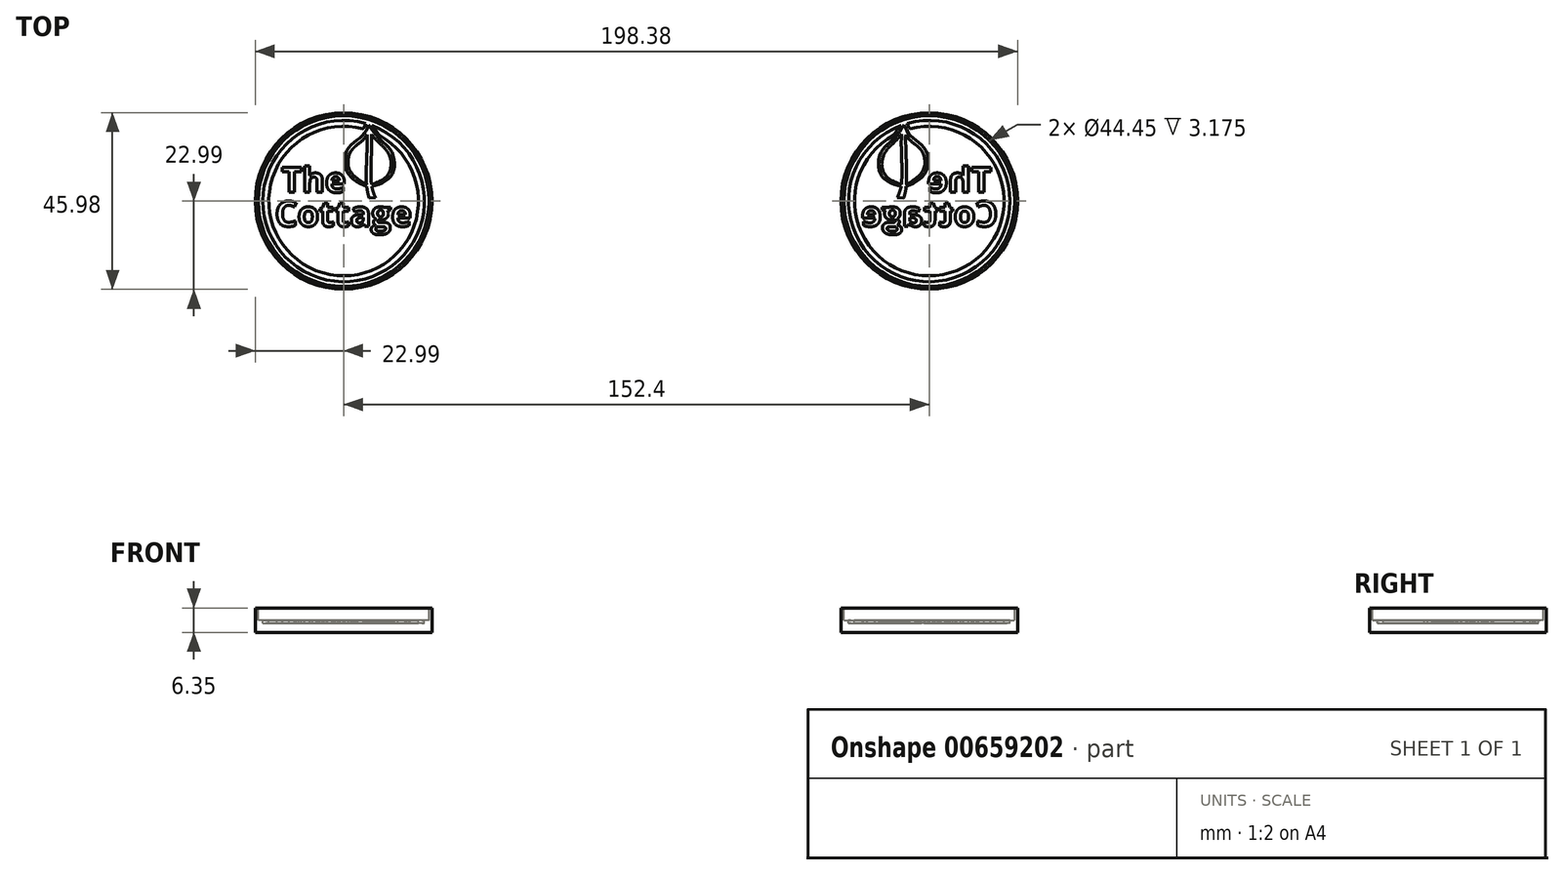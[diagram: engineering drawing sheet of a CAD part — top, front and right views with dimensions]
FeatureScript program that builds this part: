
annotation { "Feature Type Name" : "Feature", "Feature Type Description" : "" }
export const myFeature = defineFeature(function(context is Context, id is Id, definition is map)
    precondition{}
    {
        {
            var Q0;
            Q0=qCreatedBy(makeId("Top.planeOp"),FACE);
            var sketch = newSketch(context, id + "F0", { "sketchPlane" : qUnion([Q0])});
            skCircle(sketch, "E0", {"center": v(0, 0) * mm, "radius": 22.99 * mm});
            skSolve(sketch);
        }
        {
            var Q0;
            Q0 = qSketchRegion(id + "F0", true);
            extrude(context, id + "F1", {"entities" : qUnion([Q0]), "depth" : 6.35 * mm, "offsetDistance" : 25.4 * mm});
        }
        {
            var Q0;
            Q0=makeQuery(id+"F1.opExtrude","CAP_FACE",FACE,{"disambiguationData":[OSD([sQuery(id+"F0.wireOp",EDGE,"E0")])],"isStart":false});
            var sketch = newSketch(context, id + "F2", { "sketchPlane" : qUnion([Q0])});
            skCircle(sketch, "E1", {"center": v(0, 0) * mm, "radius": 22.23 * mm});
            skSolve(sketch);
        }
        {
            var Q0;
            Q0 = qSketchRegion(id + "F2", true);
            extrude(context, id + "F3", {"entities" : qUnion([Q0]), "operationType" : NewBodyOperationType.REMOVE, "oppositeDirection" : true, "depth" : 3.17 * mm, "offsetDistance" : 25.4 * mm});
        }
        {
            var Q0;
            Q0=makeQuery(id+"F3.boolean.opBoolean","COPY",FACE,{"derivedFrom":makeQuery(id+"F3.opExtrude","CAP_FACE",FACE,{"disambiguationData":[OSD([sQuery(id+"F2.wireOp",EDGE,"E1")])],"isStart":false})});
            var sketch = newSketch(context, id + "F4", { "sketchPlane" : qUnion([Q0])});
            skText(sketch, "E2", { "text": "The", "fontName": "OpenSans-Bold.ttf"});
            skText(sketch, "E3", { "text": "Cottage", "fontName": "OpenSans-Bold.ttf"});
            const initialGuessF4  = {"E2": [-0.01619, 0.00224, 1, 0, 0.0066], "E3": [-0.01786, -0.0066, 1, 0, 0.0066]};
            skSetInitialGuess(sketch, initialGuessF4);
            skSolve(sketch);
        }
        {
            var Q0;
            Q0 = qSketchRegion(id + "F4", true);
            extrude(context, id + "F5", {"entities" : qUnion([Q0]), "operationType" : NewBodyOperationType.REMOVE, "oppositeDirection" : true, "depth" : 0.76 * mm, "offsetDistance" : 25.4 * mm});
        }
        {
            var Q0;
            {var subQ0=sQuery(id+"F2.wireOp",EDGE,"E1");Q0=makeQuery(id+"F5.boolean.opBoolean","SPLIT",FACE,{"disambiguationData":[TD([makeQuery(id+"F3.boolean.opBoolean","COPY",FACE,{"derivedFrom":makeQuery(id+"F3.opExtrude","SWEPT_FACE",FACE,{"disambiguationData":[OSD([subQ0])]})})])],"derivedFrom":makeQuery(id+"F3.boolean.opBoolean","COPY",FACE,{"derivedFrom":makeQuery(id+"F3.opExtrude","CAP_FACE",FACE,{"disambiguationData":[OSD([subQ0])],"isStart":false})})});}
            var sketch = newSketch(context, id + "F6", { "sketchPlane" : qUnion([Q0])});
            skFitSpline(sketch, "E4", {"points": [v(5.96, 4.32) * mm, v(1.57, 8.06) * mm, v(1.84, 12.88) * mm, v(4.83, 15.75) * mm, v(6.61, 18.2) * mm], "startDerivative": vector(-18.93, 11.04) * mm, "endDerivative": vector(7.24, 12.22) * mm});
            skFitSpline(sketch, "E5", {"points": [v(8.3, 0.96) * mm, v(7.26, 4.32) * mm, v(7.26, 14.02) * mm, v(7.22, 17.4) * mm], "startDerivative": vector(-4.54, 9.79) * mm, "endDerivative": vector(-0.46, 10.19) * mm});
            skFitSpline(sketch, "E6", {"points": [v(8.3, 0.96) * mm, v(6.67, 0.74) * mm], "startDerivative": vector(-1.63, -0.22) * mm, "endDerivative": vector(-1.63, -0.22) * mm});
            skFitSpline(sketch, "E7", {"points": [v(7.22, 12.38) * mm, v(8.3, 13.58) * mm, v(8.98, 15.46) * mm], "startDerivative": vector(2.5, 2.3) * mm, "endDerivative": vector(1.04, 3.83) * mm});
            skFitSpline(sketch, "E8", {"points": [v(9.55, 14.9) * mm, v(9.05, 13.1) * mm, v(7.17, 11.15) * mm], "startDerivative": vector(-0.57, -4.06) * mm, "endDerivative": vector(-4.08, -3.46) * mm});
            skFitSpline(sketch, "E9", {"points": [v(7.1, 8.17) * mm, v(9.87, 10.39) * mm, v(11.25, 13.03) * mm], "startDerivative": vector(5.9, 3.93) * mm, "endDerivative": vector(2.29, 5.79) * mm});
            skFitSpline(sketch, "E10", {"points": [v(7.1, 7.13) * mm, v(9.65, 8.76) * mm, v(11.92, 11.85) * mm], "startDerivative": vector(5.64, 2.92) * mm, "endDerivative": vector(4, 6.45) * mm});
            skFitSpline(sketch, "E11", {"points": [v(6.06, 12.44) * mm, v(4.12, 14.02) * mm, v(3.6, 14.73) * mm], "startDerivative": vector(-3.62, 2.7) * mm, "endDerivative": vector(-1.1, 1.78) * mm});
            skFitSpline(sketch, "E12", {"points": [v(6.06, 11.15) * mm, v(4.5, 12.44) * mm, v(2.78, 14.02) * mm], "startDerivative": vector(-3.2, 2.6) * mm, "endDerivative": vector(-3.36, 3.13) * mm});
            skFitSpline(sketch, "E13", {"points": [v(5.91, 8.27) * mm, v(3.73, 9.84) * mm, v(1.62, 12.44) * mm], "startDerivative": vector(-4.78, 2.94) * mm, "endDerivative": vector(-3.85, 5.36) * mm});
            skFitSpline(sketch, "E14", {"points": [v(5.9, 7.13) * mm, v(3.33, 8.9) * mm, v(1.27, 11.4) * mm], "startDerivative": vector(-5.46, 3.24) * mm, "endDerivative": vector(-3.8, 5.3) * mm});
            skFitSpline(sketch, "E15.trimOffspring", {"points": [v(6.11, 17.34) * mm, v(6.11, 14.02) * mm, v(5.96, 4.32) * mm, v(6.67, 0.74) * mm], "startDerivative": vector(0.25, -10.14) * mm, "endDerivative": vector(3.15, -10.45) * mm});
            skFitSpline(sketch, "E16", {"points": [v(6.01, 3.77) * mm, v(7.34, 3.82) * mm], "startDerivative": vector(1.33, 0.05) * mm, "endDerivative": vector(1.33, 0.05) * mm});
            skFitSpline(sketch, "E17.trimOffspring", {"points": [v(6.61, 18.2) * mm, v(8.67, 15.75) * mm, v(11.92, 11.85) * mm, v(11.6, 6.92) * mm, v(7.26, 4.32) * mm], "startDerivative": vector(8.6, -11.28) * mm, "endDerivative": vector(-19.48, -7.18) * mm});
            skFitSpline(sketch, "E18", {"points": [v(7.34, 3.82) * mm, v(10.33, 4.86) * mm, v(12.5, 6.76) * mm, v(13.23, 9.67) * mm, v(12.49, 12.79) * mm, v(10.82, 14.85) * mm, v(8.8, 16.78) * mm, v(6.56, 19.8) * mm], "startDerivative": vector(21.29, 5.88) * mm, "endDerivative": vector(-13.85, 20.51) * mm});
            skFitSpline(sketch, "E19", {"points": [v(6.01, 3.77) * mm, v(2.94, 5.37) * mm, v(0.89, 7.63) * mm, v(0.32, 10.37) * mm, v(0.97, 13.35) * mm, v(3.38, 15.79) * mm, v(5.42, 17.64) * mm, v(6.56, 19.8) * mm], "startDerivative": vector(-20.9, 9.29) * mm, "endDerivative": vector(7.42, 17.7) * mm});
            skFitSpline(sketch, "E20", {"points": [v(6.06, 12.44) * mm, v(6.13, 16.15) * mm, v(6.11, 17.34) * mm], "startDerivative": vector(0.18, 6.6) * mm, "endDerivative": vector(-0.1, 2.85) * mm});
            skFitSpline(sketch, "E21", {"points": [v(6.11, 17.34) * mm, v(5, 15.86) * mm, v(3.6, 14.73) * mm], "startDerivative": vector(-2.05, -3.12) * mm, "endDerivative": vector(-2.98, -2.12) * mm});
            skFitSpline(sketch, "E22", {"points": [v(7.22, 17.4) * mm, v(8.23, 16.2) * mm, v(8.98, 15.46) * mm], "startDerivative": vector(1.9, -2.34) * mm, "endDerivative": vector(1.62, -1.53) * mm});
            skSolve(sketch);
        }
        {
            var Q0;
            Q0 = qSketchRegion(id + "F6", true);
            extrude(context, id + "F7", {"entities" : qUnion([Q0]), "operationType" : NewBodyOperationType.REMOVE, "oppositeDirection" : true, "depth" : 0.76 * mm, "offsetDistance" : 25.4 * mm});
        }
        {
            var Q0;
            {var subQ68=sQuery(id+"F2.wireOp",EDGE,"E1");var subQ69=makeQuery(id+"F3.boolean.opBoolean","COPY",FACE,{"derivedFrom":makeQuery(id+"F3.opExtrude","SWEPT_FACE",FACE,{"disambiguationData":[OSD([subQ68])]})});Q0=makeQuery(id+"F7.boolean.opBoolean","SPLIT",FACE,{"disambiguationData":[TD([subQ69])],"derivedFrom":makeQuery(id+"F5.boolean.opBoolean","SPLIT",FACE,{"disambiguationData":[TD([subQ69])],"derivedFrom":makeQuery(id+"F3.boolean.opBoolean","COPY",FACE,{"derivedFrom":makeQuery(id+"F3.opExtrude","CAP_FACE",FACE,{"disambiguationData":[OSD([subQ68])],"isStart":false})})})});}
            var sketch = newSketch(context, id + "F8", { "sketchPlane" : qUnion([Q0])});
            skArc(sketch, "E23", {"start": v(5.08, 18.8) * mm, "mid": v(-7.2, -18.09) * mm, "end": v(9.24, 17.14) * mm});
            skArc(sketch, "E24", {"start": v(5.73, 20.21) * mm, "mid": v(-6.54, -19.96) * mm, "end": v(7.34, 19.68) * mm});
            skFitSpline(sketch, "E25", {"points": [v(5.08, 18.8) * mm, v(5.45, 19.49) * mm, v(5.73, 20.21) * mm], "startDerivative": vector(0.79, 1.35) * mm, "endDerivative": vector(0.51, 1.45) * mm});
            skFitSpline(sketch, "E26", {"points": [v(9.24, 17.14) * mm, v(8.16, 18.67) * mm, v(7.34, 19.68) * mm], "startDerivative": vector(-2, 3) * mm, "endDerivative": vector(-1.79, 2.09) * mm});
            skSolve(sketch);
        }
        {
            var Q0;
            Q0 = qSketchRegion(id + "F8", true);
            extrude(context, id + "F9", {"entities" : qUnion([Q0]), "operationType" : NewBodyOperationType.REMOVE, "oppositeDirection" : true, "depth" : 0.76 * mm, "offsetDistance" : 25.4 * mm});
        }
        {
            var Q0;
            Q0=qCreatedBy(makeId("Right.planeOp"),FACE);
            cPlane(context, id + "F10", {"entities" : qUnion([Q0]), "cplaneType" : CPlaneType.OFFSET, "offset" : 76.2 * mm, "width" : 152.4 * mm, "height" : 152.4 * mm});
        }
        {
            var Q0;
            Q0=makeQuery(id+"F1.opExtrude","SWEPT_BODY",BODY,{"disambiguationData":[OSD([sQuery(id+"F0.wireOp",EDGE,"E0")])]});
            var Q1;
            Q1=qCreatedBy(id+"F10.planeOp",FACE);
            mirror(context, id + "F11", {"entities" : qUnion([Q0]), "mirrorPlane" : qUnion([Q1])});
        }
    });
